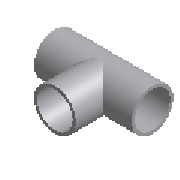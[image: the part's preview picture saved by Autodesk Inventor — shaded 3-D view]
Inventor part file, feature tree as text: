
AUTODESK INVENTOR PART (.ipt)
format: ipt  version: 2025.1 (Build 291241020, 241B)  size: 170,496 bytes
history: native  units: mm (DEFAULTED — no unit token found)
features: other x6, extrude x4
ambient origin geometry x8: Origin, YZ Plane, XZ Plane, XY Plane, X Axis, Y Axis, Z Axis, Center Point
bodies: Solid1 (feature_tree)
feature tree (10):
  extrude  "Extrude1"  Depth=88.9mm
  extrude  "Extrude2"  Depth=172.0mm
  extrude  "Extrude3"  TaperAngle=0.0deg  [1 undecoded]
  extrude  "Extrude4"  Depth=88.9mm
  other  "Work Axis1"
  other  "Work Point1"
  other  "Work Axis2"
  other  "Work Point2"
  other  "Work Axis3"
  other  "Work Point3"
note: 1 required parameter value undecoded (feature->parameter linkage not recoverable at this tier; creation-order binding heuristic only, values carry confidence <= 0.55)
